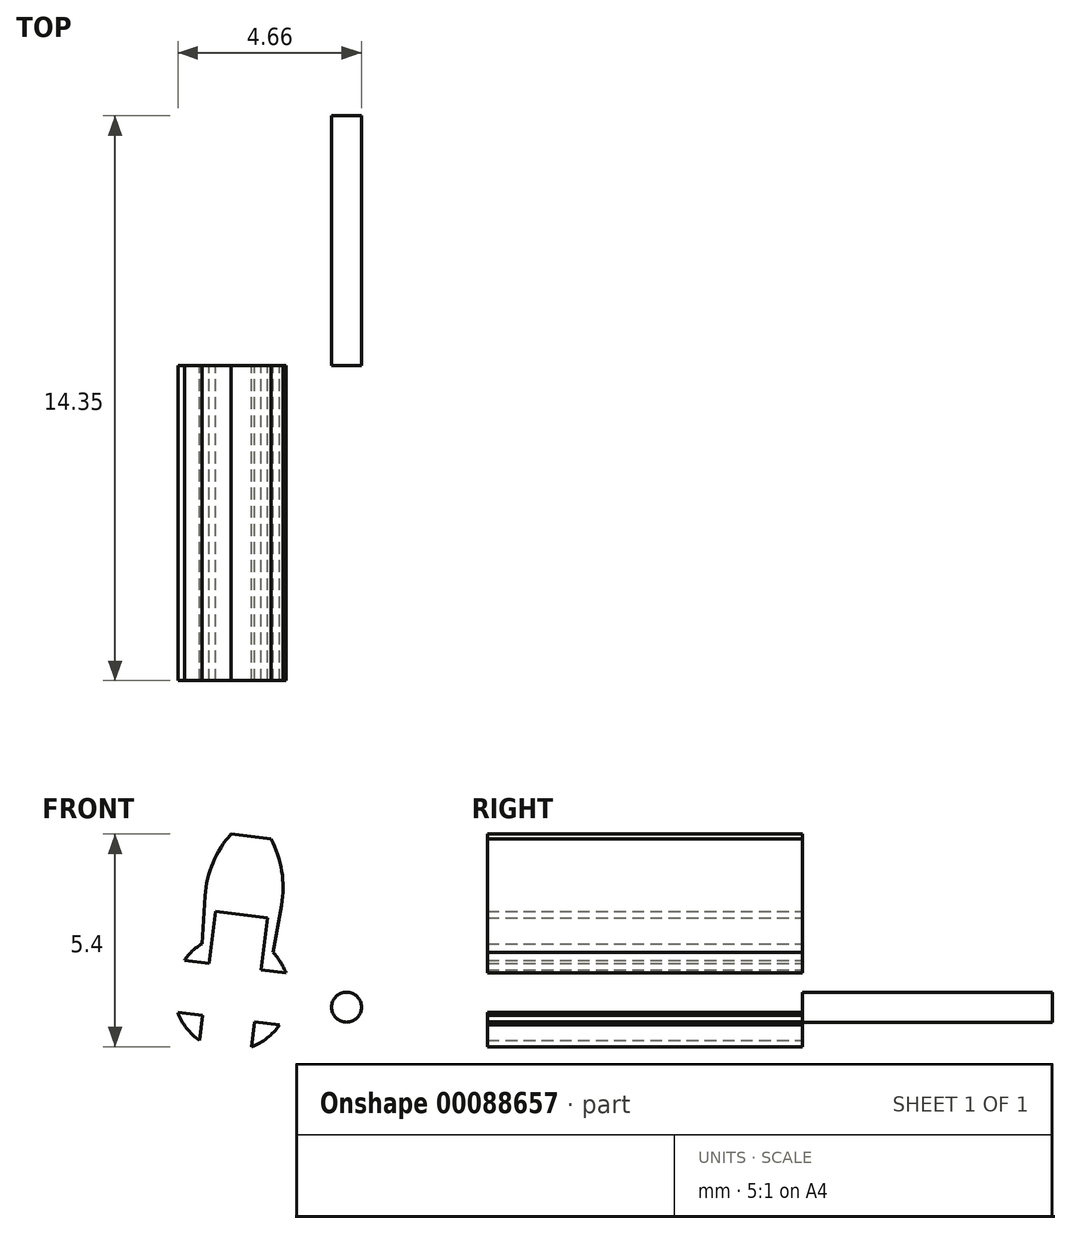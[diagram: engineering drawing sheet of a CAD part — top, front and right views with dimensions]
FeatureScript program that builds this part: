
annotation { "Feature Type Name" : "Feature", "Feature Type Description" : "" }
export const myFeature = defineFeature(function(context is Context, id is Id, definition is map)
    precondition{}
    {
        {
            var Q0;
            Q0=qCreatedBy(makeId("Front.planeOp"),FACE);
            var sketch = newSketch(context, id + "F0", { "sketchPlane" : qUnion([Q0])});
            skLineSegment(sketch, "E0", {"start": v(-0.02, 4.03) * mm, "end": v(1, 3.9) * mm});
            skArc(sketch, "E1", {"start": v(-0.76, 1.25) * mm, "mid": v(0.18, 1.45) * mm, "end": v(1.04, 1.03) * mm});
            skLineSegment(sketch, "E2", {"start": v(-0.68, 2.46) * mm, "end": v(-0.76, 1.25) * mm});
            skLineSegment(sketch, "E3.MirrorCS", {"start": v(1.26, 2.23) * mm, "end": v(1.04, 1.03) * mm});
            skLineSegment(sketch, "E4", {"start": v(0.18, 1.45) * mm, "end": v(0.52, 4.26) * mm, "construction": true});
            skArc(sketch, "E5", {"start": v(-0.02, 4.03) * mm, "mid": v(-0.48, 3.3) * mm, "end": v(-0.68, 2.46) * mm});
            skArc(sketch, "E6", {"start": v(1.26, 2.23) * mm, "mid": v(1.27, 3.09) * mm, "end": v(1, 3.9) * mm});
            skSolve(sketch);
        }
        {
            var Q0;
            Q0=qCreatedBy(makeId("Top.planeOp"),FACE);
            var sketch = newSketch(context, id + "F1", { "sketchPlane" : qUnion([Q0])});
            skLineSegment(sketch, "E7", {"start": v(0, 0) * mm, "end": v(0, 30.53) * mm, "construction": true});
            skLineSegment(sketch, "E8", {"start": v(0, 0) * mm, "end": v(0, -25.91) * mm, "construction": true});
            skSolve(sketch);
        }
        {
            var Q0;
            Q0=qCreatedBy(makeId("Front.planeOp"),FACE);
            var sketch = newSketch(context, id + "F2", { "sketchPlane" : qUnion([Q0])});
            skCircle(sketch, "E9", {"center": v(0, 0) * mm, "radius": 1.46 * mm});
            skSolve(sketch);
        }
        {
            var Q0;
            Q0=makeQuery(id+"F2.imprint","IMPRINT",FACE,{"disambiguationData":[TD([[makeQuery(id+"F2.imprint","IMPRINT",EDGE,{"derivedFrom":sQuery(id+"F2.wireOp",EDGE,"E9")}),1.0]])]});
            extrude(context, id + "F3", {"entities" : qUnion([Q0]), "depth" : 8 * mm});
        }
        {
            var Q0;
            Q0=makeQuery(id+"F0.imprint","IMPRINT",FACE,{"disambiguationData":[TD([[makeQuery(id+"F0.imprint","IMPRINT",EDGE,{"derivedFrom":sQuery(id+"F0.wireOp",EDGE,"E0")}),-1.0]])]});
            var Q1;
            Q1=makeQuery(id+"F3.opExtrude","CAP_FACE",FACE,{"disambiguationData":[OSD([sQuery(id+"F2.wireOp",EDGE,"E9"),sQuery(id+"F2.wireOp",EDGE,"arTuxXPW-NgsZ-czPZ-2IIf-RW4LCaOOxTTB"),sQuery(id+"F2.wireOp",EDGE,"3ab69d48-fd6e-4c46-9385-d5405a46b24b.1.0.0"),sQuery(id+"F2.wireOp",EDGE,"6b936541-0af8-4921-b432-69622a55d935.0.1.0"),sQuery(id+"F2.wireOp",EDGE,"ef216592-30cf-427c-a956-27d8a622ba70.1.0.0")])],"isStart":false});
            extrude(context, id + "F4", {"entities" : qUnion([Q0]), "operationType" : NewBodyOperationType.ADD, "endBound" : BoundingType.UP_TO_SURFACE, "endBoundEntityFace" : qUnion([Q1]), "depth" : 25.4 * mm});
        }
        {
            var Q0;
            Q0=qCreatedBy(makeId("Front.planeOp"),FACE);
            var sketch = newSketch(context, id + "F5", { "sketchPlane" : qUnion([Q0])});
            skLineSegment(sketch, "E10", {"start": v(0.49, 3.97) * mm, "end": v(-0.49, -3.97) * mm, "construction": true});
            skLineSegment(sketch, "E11", {"start": v(0.9, 1.9) * mm, "end": v(0.74, 0.58) * mm});
            skLineSegment(sketch, "E12", {"start": v(0.74, 0.58) * mm, "end": v(2.07, 0.42) * mm});
            skLineSegment(sketch, "E13", {"start": v(2.07, 0.42) * mm, "end": v(1.99, -0.24) * mm});
            skLineSegment(sketch, "E14", {"start": v(0.9, 1.9) * mm, "end": v(0.24, 1.99) * mm});
            skLineSegment(sketch, "E15", {"start": v(3.97, -0.49) * mm, "end": v(-1.87, 0.23) * mm, "construction": true});
            skLineSegment(sketch, "E16.MirrorCS", {"start": v(0.42, -2.07) * mm, "end": v(-0.24, -1.99) * mm});
            skLineSegment(sketch, "E17.MirrorCS", {"start": v(0.42, -2.07) * mm, "end": v(0.58, -0.74) * mm});
            skLineSegment(sketch, "E18.MirrorCS", {"start": v(0.58, -0.74) * mm, "end": v(1.9, -0.9) * mm});
            skLineSegment(sketch, "E19.MirrorCS", {"start": v(1.9, -0.9) * mm, "end": v(1.99, -0.24) * mm});
            skLineSegment(sketch, "E20.MirrorCS", {"start": v(-0.42, 2.07) * mm, "end": v(0.24, 1.99) * mm});
            skLineSegment(sketch, "E21.MirrorCS", {"start": v(-0.42, 2.07) * mm, "end": v(-0.58, 0.74) * mm});
            skLineSegment(sketch, "E22.MirrorCS", {"start": v(-0.58, 0.74) * mm, "end": v(-1.9, 0.9) * mm});
            skLineSegment(sketch, "E23.MirrorCS", {"start": v(-1.9, 0.9) * mm, "end": v(-1.99, 0.24) * mm});
            skLineSegment(sketch, "E24.MirrorCS", {"start": v(-2.07, -0.42) * mm, "end": v(-1.99, 0.24) * mm});
            skLineSegment(sketch, "E25.MirrorCS", {"start": v(-0.74, -0.58) * mm, "end": v(-2.07, -0.42) * mm});
            skLineSegment(sketch, "E26.MirrorCS", {"start": v(-0.9, -1.9) * mm, "end": v(-0.74, -0.58) * mm});
            skLineSegment(sketch, "E27.MirrorCS", {"start": v(-0.9, -1.9) * mm, "end": v(-0.24, -1.99) * mm});
            skSolve(sketch);
        }
        {
            var Q0;
            Q0 = qSketchRegion(id + "F5", true);
            extrude(context, id + "F6", {"entities" : qUnion([Q0]), "operationType" : NewBodyOperationType.REMOVE, "depth" : 25.4 * mm});
        }
        {
            var Q0;
            Q0=qCreatedBy(makeId("Front.planeOp"),FACE);
            var sketch = newSketch(context, id + "F7", { "sketchPlane" : qUnion([Q0])});
            skCircle(sketch, "E28", {"center": v(2.91, -0.37) * mm, "radius": 0.38 * mm});
            skSolve(sketch);
        }
        {
            var Q0;
            Q0 = qSketchRegion(id + "F7", true);
            extrude(context, id + "F8", {"entities" : qUnion([Q0]), "operationType" : NewBodyOperationType.ADD, "oppositeDirection" : true, "depth" : 6.35 * mm});
        }
    });
